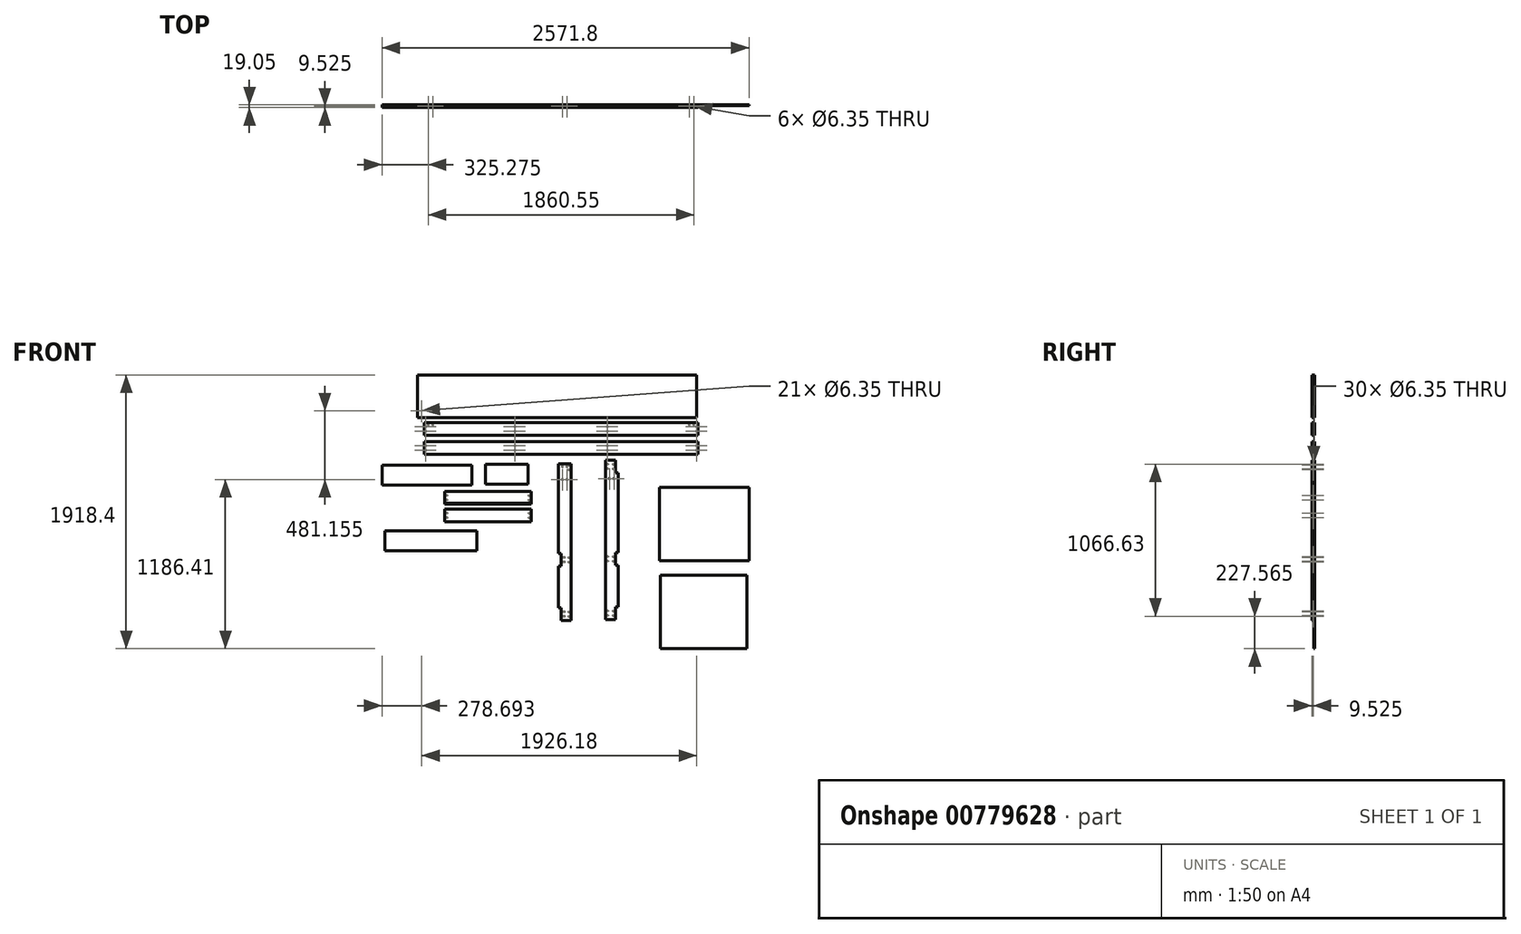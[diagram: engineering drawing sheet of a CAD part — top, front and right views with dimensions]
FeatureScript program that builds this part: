
annotation { "Feature Type Name" : "Feature", "Feature Type Description" : "" }
export const myFeature = defineFeature(function(context is Context, id is Id, definition is map)
    precondition{}
    {
        {
            var Q0;
            Q0=qCreatedBy(makeId("Front.planeOp"),FACE);
            var sketch = newSketch(context, id + "F0", { "sketchPlane" : qUnion([Q0])});
            skLineSegment(sketch, "E0.bottom", {"start": v(-0.42, -594.36) * mm, "end": v(69.43, -594.36) * mm});
            skLineSegment(sketch, "E0.left", {"start": v(-19.47, -505.46) * mm, "end": v(-19.47, -213.36) * mm});
            skLineSegment(sketch, "E0.right", {"start": v(69.43, -594.36) * mm, "end": v(69.43, 504.2) * mm});
            skLineSegment(sketch, "E1", {"start": v(-0.42, -594.36) * mm, "end": v(-0.42, -505.46) * mm});
            skLineSegment(sketch, "E2", {"start": v(-0.42, -505.46) * mm, "end": v(-19.47, -505.46) * mm});
            skLineSegment(sketch, "E3", {"start": v(-0.42, -213.36) * mm, "end": v(-19.47, -213.36) * mm});
            skLineSegment(sketch, "E4", {"start": v(-0.42, -213.36) * mm, "end": v(-0.42, -124.46) * mm});
            skLineSegment(sketch, "E5", {"start": v(-0.42, -124.46) * mm, "end": v(-19.47, -124.46) * mm});
            skLineSegment(sketch, "E6", {"start": v(-19.47, 504.2) * mm, "end": v(69.43, 504.2) * mm});
            skLineSegment(sketch, "E7", {"start": v(-19.47, -124.46) * mm, "end": v(-19.47, 504.2) * mm});
            skLineSegment(sketch, "E8", {"start": v(-0.42, -213.36) * mm, "end": v(69.43, -213.36) * mm});
            skLineSegment(sketch, "E9", {"start": v(-0.42, -124.46) * mm, "end": v(69.43, -124.46) * mm});
            skPoint(sketch, "E10", {"position": v(9.1, 393.07) * mm});
            skPoint(sketch, "E11", {"position": v(40.85, 393.07) * mm});
            skSolve(sketch);
        }
        {
            var Q0;
            Q0=qCreatedBy(makeId("Front.planeOp"),FACE);
            var sketch = newSketch(context, id + "F1", { "sketchPlane" : qUnion([Q0])});
            skLineSegment(sketch, "E12.right", {"start": v(309.74, -588.17) * mm, "end": v(309.74, 529.43) * mm});
            skLineSegment(sketch, "E13.MirrorCS", {"start": v(398.64, 440.53) * mm, "end": v(379.59, 440.53) * mm});
            skLineSegment(sketch, "E14.MirrorCS", {"start": v(379.59, -207.17) * mm, "end": v(398.64, -207.17) * mm});
            skLineSegment(sketch, "E15.MirrorCS", {"start": v(379.59, -499.27) * mm, "end": v(398.64, -499.27) * mm});
            skLineSegment(sketch, "E16.MirrorCS", {"start": v(379.59, -207.17) * mm, "end": v(379.59, -118.27) * mm});
            skLineSegment(sketch, "E17.MirrorCS", {"start": v(379.59, 440.53) * mm, "end": v(379.59, 529.43) * mm});
            skLineSegment(sketch, "E18.MirrorCS", {"start": v(379.59, -588.17) * mm, "end": v(379.59, -499.27) * mm});
            skLineSegment(sketch, "E19.MirrorCS", {"start": v(379.59, 529.43) * mm, "end": v(309.74, 529.43) * mm});
            skLineSegment(sketch, "E20.MirrorCS", {"start": v(379.59, -118.27) * mm, "end": v(398.64, -118.27) * mm});
            skLineSegment(sketch, "E21.MirrorCS", {"start": v(379.59, -588.17) * mm, "end": v(309.74, -588.17) * mm});
            skLineSegment(sketch, "E22.MirrorCS", {"start": v(398.64, -499.27) * mm, "end": v(398.64, -207.17) * mm});
            skLineSegment(sketch, "E23", {"start": v(398.64, -118.27) * mm, "end": v(398.64, 440.53) * mm});
            skLineSegment(sketch, "E24", {"start": v(379.59, -118.27) * mm, "end": v(309.74, -118.27) * mm});
            skLineSegment(sketch, "E25", {"start": v(379.59, -207.17) * mm, "end": v(309.74, -207.17) * mm});
            skPoint(sketch, "E26", {"position": v(338.31, 399.25) * mm});
            skPoint(sketch, "E27", {"position": v(370.06, 399.25) * mm});
            skSolve(sketch);
        }
        {
            var Q0;
            Q0=makeQuery(id+"F0.imprint","IMPRINT",FACE,{"disambiguationData":[TD([[makeQuery(id+"F0.imprint","IMPRINT",EDGE,{"derivedFrom":sQuery(id+"F0.wireOp",EDGE,"E0.bottom")}),1.0]])]});
            var Q1;
            Q1=makeQuery(id+"F0.imprint","IMPRINT",FACE,{"disambiguationData":[TD([[makeQuery(id+"F0.imprint","IMPRINT",EDGE,{"derivedFrom":sQuery(id+"F0.wireOp",EDGE,"E4")}),-1.0]])]});
            var Q2;
            Q2=makeQuery(id+"F0.imprint","IMPRINT",FACE,{"disambiguationData":[TD([[makeQuery(id+"F0.imprint","IMPRINT",EDGE,{"derivedFrom":sQuery(id+"F0.wireOp",EDGE,"E5")}),-1.0]])]});
            extrude(context, id + "F2", {"entities" : qUnion([Q0, Q1, Q2]), "depth" : 19.05 * mm, "offsetDistance" : 25.4 * mm});
        }
        {
            var Q0;
            Q0=makeQuery(id+"F1.imprint","IMPRINT",FACE,{"disambiguationData":[TD([[makeQuery(id+"F1.imprint","IMPRINT",EDGE,{"derivedFrom":sQuery(id+"F1.wireOp",EDGE,"E12.right")}),-1.0]])]});
            var Q1;
            Q1=makeQuery(id+"F1.imprint","IMPRINT",FACE,{"disambiguationData":[TD([[makeQuery(id+"F1.imprint","IMPRINT",EDGE,{"derivedFrom":sQuery(id+"F1.wireOp",EDGE,"E14.MirrorCS")}),-1.0]])]});
            var Q2;
            Q2=makeQuery(id+"F1.imprint","IMPRINT",FACE,{"disambiguationData":[TD([[makeQuery(id+"F1.imprint","IMPRINT",EDGE,{"derivedFrom":sQuery(id+"F1.wireOp",EDGE,"E13.MirrorCS")}),1.0]])]});
            extrude(context, id + "F3", {"entities" : qUnion([Q0, Q1, Q2]), "depth" : 19.05 * mm, "offsetDistance" : 25.4 * mm});
        }
        {
            var Q0;
            Q0=makeQuery(id+"F2.opExtrude","SWEPT_FACE",FACE,{"disambiguationData":[OSD([sQuery(id+"F0.wireOp",EDGE,"E1")])]});
            var sketch = newSketch(context, id + "F4", { "sketchPlane" : qUnion([Q0])});
            skLineSegment(sketch, "E28.0.0", {"start": v(0, -505.46) * mm, "end": v(0, -594.36) * mm});
            skLineSegment(sketch, "E28.0.1", {"start": v(0, -594.36) * mm, "end": v(19.05, -594.36) * mm});
            skLineSegment(sketch, "E28.0.2", {"start": v(19.05, -594.36) * mm, "end": v(19.05, -505.46) * mm});
            skLineSegment(sketch, "E28.0.3", {"start": v(19.05, -505.46) * mm, "end": v(0, -505.46) * mm});
            skPoint(sketch, "E29", {"position": v(9.53, -534.03) * mm});
            skPoint(sketch, "E29.positionSnap0", {"position": v(9.53, -505.46) * mm});
            skPoint(sketch, "E30", {"position": v(9.52, -565.78) * mm});
            skPoint(sketch, "E30.positionSnap0", {"position": v(9.53, -594.36) * mm});
            skSolve(sketch);
        }
        {
            var Q0;
            Q0=sQuery(id+"F4.wireOp",VERTEX,"E29");
            var Q1;
            Q1=sQuery(id+"F4.wireOp",VERTEX,"E30");
            var Q2;
            Q2=makeQuery(id+"F2.opExtrude","SWEPT_BODY",BODY,{"disambiguationData":[OSD([sQuery(id+"F0.wireOp",EDGE,"E0.bottom"),sQuery(id+"F0.wireOp",EDGE,"E0.left"),sQuery(id+"F0.wireOp",EDGE,"E0.right"),sQuery(id+"F0.wireOp",EDGE,"E1"),sQuery(id+"F0.wireOp",EDGE,"E2"),sQuery(id+"F0.wireOp",EDGE,"E3"),sQuery(id+"F0.wireOp",EDGE,"E4"),sQuery(id+"F0.wireOp",EDGE,"E5"),sQuery(id+"F0.wireOp",EDGE,"E6"),sQuery(id+"F0.wireOp",EDGE,"E7")])]});
            hole(context, id + "F5", {"style" : HoleStyle.SIMPLE, "endStyle" : HoleEndStyle.BLIND, "holeDiameter" : 6.35 * mm, "majorDiameter" : 6.35 * mm, "holeDepth" : 25.4 * mm, "isTappedThrough" : true, "tappedDepth" : 12.7 * mm, "tapClearance" : 3, "locations" : qUnion([Q0, Q1]), "scope" : qUnion([Q2])});
        }
        {
            var Q0;
            Q0=makeQuery(id+"F2.opExtrude","SWEPT_FACE",FACE,{"disambiguationData":[OSD([sQuery(id+"F0.wireOp",EDGE,"E4")])]});
            var sketch = newSketch(context, id + "F6", { "sketchPlane" : qUnion([Q0])});
            skLineSegment(sketch, "E31.0.0", {"start": v(0, -124.46) * mm, "end": v(0, -213.36) * mm});
            skLineSegment(sketch, "E31.0.1", {"start": v(0, -213.36) * mm, "end": v(19.05, -213.36) * mm});
            skLineSegment(sketch, "E31.0.2", {"start": v(19.05, -213.36) * mm, "end": v(19.05, -124.46) * mm});
            skLineSegment(sketch, "E31.0.3", {"start": v(19.05, -124.46) * mm, "end": v(0, -124.46) * mm});
            skPoint(sketch, "E32", {"position": v(9.53, -153.04) * mm});
            skPoint(sketch, "E32.positionSnap0", {"position": v(9.53, -124.46) * mm});
            skPoint(sketch, "E33", {"position": v(9.53, -184.79) * mm});
            skPoint(sketch, "E33.positionSnap0", {"position": v(9.53, -213.36) * mm});
            skSolve(sketch);
        }
        {
            var Q0;
            Q0=sQuery(id+"F6.wireOp",VERTEX,"E32");
            var Q1;
            Q1=sQuery(id+"F6.wireOp",VERTEX,"E33");
            var Q2;
            Q2=makeQuery(id+"F2.opExtrude","SWEPT_BODY",BODY,{"disambiguationData":[OSD([sQuery(id+"F0.wireOp",EDGE,"E0.bottom"),sQuery(id+"F0.wireOp",EDGE,"E0.left"),sQuery(id+"F0.wireOp",EDGE,"E0.right"),sQuery(id+"F0.wireOp",EDGE,"E1"),sQuery(id+"F0.wireOp",EDGE,"E2"),sQuery(id+"F0.wireOp",EDGE,"E3"),sQuery(id+"F0.wireOp",EDGE,"E4"),sQuery(id+"F0.wireOp",EDGE,"E5"),sQuery(id+"F0.wireOp",EDGE,"E6"),sQuery(id+"F0.wireOp",EDGE,"E7")])]});
            hole(context, id + "F7", {"style" : HoleStyle.SIMPLE, "endStyle" : HoleEndStyle.BLIND, "holeDiameter" : 6.35 * mm, "majorDiameter" : 6.35 * mm, "holeDepth" : 25.4 * mm, "isTappedThrough" : true, "tappedDepth" : 12.7 * mm, "tapClearance" : 3, "locations" : qUnion([Q0, Q1]), "scope" : qUnion([Q2])});
        }
        {
            var Q0;
            Q0=makeQuery(id+"F2.opExtrude","SWEPT_FACE",FACE,{"disambiguationData":[OSD([sQuery(id+"F0.wireOp",EDGE,"E0.right")])]});
            var sketch = newSketch(context, id + "F8", { "sketchPlane" : qUnion([Q0])});
            skLineSegment(sketch, "E34.0.0", {"start": v(0, -594.36) * mm, "end": v(0, 504.2) * mm});
            skLineSegment(sketch, "E34.0.1", {"start": v(0, 504.2) * mm, "end": v(-19.05, 504.2) * mm});
            skLineSegment(sketch, "E34.0.2", {"start": v(-19.05, 504.2) * mm, "end": v(-19.05, -594.36) * mm});
            skLineSegment(sketch, "E34.0.3", {"start": v(-19.05, -594.36) * mm, "end": v(0, -594.36) * mm});
            skPoint(sketch, "E35", {"position": v(-9.53, 494.67) * mm});
            skPoint(sketch, "E35.positionSnap0", {"position": v(-9.53, 504.2) * mm});
            skPoint(sketch, "E36", {"position": v(-9.53, 462.92) * mm});
            skPoint(sketch, "E37", {"position": v(-9.53, -565.78) * mm});
            skPoint(sketch, "E37.positionSnap0", {"position": v(-9.53, -594.36) * mm});
            skPoint(sketch, "E38", {"position": v(-9.53, -534.03) * mm});
            skPoint(sketch, "E39.0", {"position": v(0, -124.46) * mm});
            skPoint(sketch, "E40.0", {"position": v(0, -213.36) * mm});
            skPoint(sketch, "E41", {"position": v(-9.53, -213.36) * mm});
            skPoint(sketch, "E42", {"position": v(-9.53, -184.79) * mm});
            skPoint(sketch, "E43", {"position": v(-9.53, -153.04) * mm});
            skSolve(sketch);
        }
        {
            var Q0;
            Q0=sQuery(id+"F8.wireOp",VERTEX,"E35");
            var Q1;
            Q1=sQuery(id+"F8.wireOp",VERTEX,"E36");
            var Q2;
            Q2=sQuery(id+"F8.wireOp",VERTEX,"E37");
            var Q3;
            Q3=sQuery(id+"F8.wireOp",VERTEX,"E38");
            var Q4;
            Q4=sQuery(id+"F8.wireOp",VERTEX,"E42");
            var Q5;
            Q5=sQuery(id+"F8.wireOp",VERTEX,"E43");
            var Q6;
            Q6=makeQuery(id+"F2.opExtrude","SWEPT_BODY",BODY,{"disambiguationData":[OSD([sQuery(id+"F0.wireOp",EDGE,"E0.bottom"),sQuery(id+"F0.wireOp",EDGE,"E0.left"),sQuery(id+"F0.wireOp",EDGE,"E0.right"),sQuery(id+"F0.wireOp",EDGE,"E1"),sQuery(id+"F0.wireOp",EDGE,"E2"),sQuery(id+"F0.wireOp",EDGE,"E3"),sQuery(id+"F0.wireOp",EDGE,"E4"),sQuery(id+"F0.wireOp",EDGE,"E5"),sQuery(id+"F0.wireOp",EDGE,"E6"),sQuery(id+"F0.wireOp",EDGE,"E7")])]});
            hole(context, id + "F9", {"style" : HoleStyle.SIMPLE, "endStyle" : HoleEndStyle.BLIND, "holeDiameter" : 6.35 * mm, "majorDiameter" : 6.35 * mm, "holeDepth" : 19.05 * mm, "isTappedThrough" : true, "tappedDepth" : 12.7 * mm, "tapClearance" : 3, "locations" : qUnion([Q0, Q1, Q2, Q3, Q4, Q5]), "scope" : qUnion([Q6])});
        }
        {
            var Q0;
            Q0=makeQuery(id+"F2.opExtrude","SWEPT_FACE",FACE,{"disambiguationData":[OSD([sQuery(id+"F0.wireOp",EDGE,"E6")])]});
            var sketch = newSketch(context, id + "F10", { "sketchPlane" : qUnion([Q0])});
            skLineSegment(sketch, "E44.0.0", {"start": v(69.43, 0) * mm, "end": v(-19.47, 0) * mm});
            skLineSegment(sketch, "E44.0.1", {"start": v(-19.47, 0) * mm, "end": v(-19.47, -19.05) * mm});
            skLineSegment(sketch, "E44.0.2", {"start": v(-19.47, -19.05) * mm, "end": v(69.43, -19.05) * mm});
            skLineSegment(sketch, "E44.0.3", {"start": v(69.43, -19.05) * mm, "end": v(69.43, 0) * mm});
            skPoint(sketch, "E45", {"position": v(9.1, -9.53) * mm});
            skPoint(sketch, "E45.positionSnap0", {"position": v(-19.47, -9.53) * mm});
            skPoint(sketch, "E46", {"position": v(40.85, -9.53) * mm});
            skSolve(sketch);
        }
        {
            var Q0;
            Q0=sQuery(id+"F10.wireOp",VERTEX,"E45");
            var Q1;
            Q1=sQuery(id+"F10.wireOp",VERTEX,"E46");
            var Q2;
            Q2=makeQuery(id+"F2.opExtrude","SWEPT_BODY",BODY,{"disambiguationData":[OSD([sQuery(id+"F0.wireOp",EDGE,"E0.bottom"),sQuery(id+"F0.wireOp",EDGE,"E0.left"),sQuery(id+"F0.wireOp",EDGE,"E0.right"),sQuery(id+"F0.wireOp",EDGE,"E1"),sQuery(id+"F0.wireOp",EDGE,"E2"),sQuery(id+"F0.wireOp",EDGE,"E3"),sQuery(id+"F0.wireOp",EDGE,"E4"),sQuery(id+"F0.wireOp",EDGE,"E5"),sQuery(id+"F0.wireOp",EDGE,"E6"),sQuery(id+"F0.wireOp",EDGE,"E7")])]});
            hole(context, id + "F11", {"style" : HoleStyle.SIMPLE, "endStyle" : HoleEndStyle.BLIND, "holeDiameter" : 6.35 * mm, "majorDiameter" : 6.35 * mm, "holeDepth" : 25.4 * mm, "isTappedThrough" : true, "tappedDepth" : 12.7 * mm, "tapClearance" : 3, "locations" : qUnion([Q0, Q1]), "scope" : qUnion([Q2])});
        }
        {
            var Q0;
            Q0=makeQuery(id+"F3.opExtrude","SWEPT_FACE",FACE,{"disambiguationData":[OSD([sQuery(id+"F1.wireOp",EDGE,"E17.MirrorCS")])]});
            var sketch = newSketch(context, id + "F12", { "sketchPlane" : qUnion([Q0])});
            skLineSegment(sketch, "E47.0.0", {"start": v(0, 440.53) * mm, "end": v(0, 529.43) * mm});
            skLineSegment(sketch, "E47.0.1", {"start": v(0, 529.43) * mm, "end": v(-19.05, 529.43) * mm});
            skLineSegment(sketch, "E47.0.2", {"start": v(-19.05, 529.43) * mm, "end": v(-19.05, 440.53) * mm});
            skLineSegment(sketch, "E47.0.3", {"start": v(-19.05, 440.53) * mm, "end": v(0, 440.53) * mm});
            skPoint(sketch, "E48", {"position": v(-9.53, 529.43) * mm});
            skPoint(sketch, "E49", {"position": v(-9.53, 500.85) * mm});
            skPoint(sketch, "E50", {"position": v(-9.53, 469.1) * mm});
            skSolve(sketch);
        }
        {
            var Q0;
            Q0=sQuery(id+"F12.wireOp",VERTEX,"E49");
            var Q1;
            Q1=sQuery(id+"F12.wireOp",VERTEX,"E50");
            var Q2;
            Q2=makeQuery(id+"F3.opExtrude","SWEPT_BODY",BODY,{"disambiguationData":[OSD([sQuery(id+"F1.wireOp",EDGE,"E12.right"),sQuery(id+"F1.wireOp",EDGE,"E13.MirrorCS"),sQuery(id+"F1.wireOp",EDGE,"E14.MirrorCS"),sQuery(id+"F1.wireOp",EDGE,"E15.MirrorCS"),sQuery(id+"F1.wireOp",EDGE,"E16.MirrorCS"),sQuery(id+"F1.wireOp",EDGE,"E17.MirrorCS"),sQuery(id+"F1.wireOp",EDGE,"E18.MirrorCS"),sQuery(id+"F1.wireOp",EDGE,"E19.MirrorCS"),sQuery(id+"F1.wireOp",EDGE,"E20.MirrorCS"),sQuery(id+"F1.wireOp",EDGE,"E21.MirrorCS"),sQuery(id+"F1.wireOp",EDGE,"E22.MirrorCS"),sQuery(id+"F1.wireOp",EDGE,"E23")])]});
            hole(context, id + "F13", {"style" : HoleStyle.SIMPLE, "endStyle" : HoleEndStyle.BLIND, "holeDiameter" : 6.35 * mm, "majorDiameter" : 6.35 * mm, "holeDepth" : 19.05 * mm, "isTappedThrough" : true, "tappedDepth" : 12.7 * mm, "tapClearance" : 3, "locations" : qUnion([Q0, Q1]), "scope" : qUnion([Q2])});
        }
        {
            var Q0;
            Q0=makeQuery(id+"F3.opExtrude","SWEPT_FACE",FACE,{"disambiguationData":[OSD([sQuery(id+"F1.wireOp",EDGE,"E16.MirrorCS")])]});
            var sketch = newSketch(context, id + "F14", { "sketchPlane" : qUnion([Q0])});
            skLineSegment(sketch, "E51.0.0", {"start": v(0, -207.17) * mm, "end": v(0, -118.27) * mm});
            skLineSegment(sketch, "E51.0.1", {"start": v(0, -118.27) * mm, "end": v(-19.05, -118.27) * mm});
            skLineSegment(sketch, "E51.0.2", {"start": v(-19.05, -118.27) * mm, "end": v(-19.05, -207.17) * mm});
            skLineSegment(sketch, "E51.0.3", {"start": v(-19.05, -207.17) * mm, "end": v(0, -207.17) * mm});
            skPoint(sketch, "E52", {"position": v(-9.53, -118.27) * mm});
            skPoint(sketch, "E53", {"position": v(-9.53, -146.85) * mm});
            skPoint(sketch, "E54", {"position": v(-9.53, -207.17) * mm});
            skPoint(sketch, "E55", {"position": v(-9.53, -178.6) * mm});
            skSolve(sketch);
        }
        {
            var Q0;
            Q0=sQuery(id+"F14.wireOp",VERTEX,"E53");
            var Q1;
            Q1=sQuery(id+"F14.wireOp",VERTEX,"E55");
            var Q2;
            Q2=makeQuery(id+"F3.opExtrude","SWEPT_BODY",BODY,{"disambiguationData":[OSD([sQuery(id+"F1.wireOp",EDGE,"E12.right"),sQuery(id+"F1.wireOp",EDGE,"E13.MirrorCS"),sQuery(id+"F1.wireOp",EDGE,"E14.MirrorCS"),sQuery(id+"F1.wireOp",EDGE,"E15.MirrorCS"),sQuery(id+"F1.wireOp",EDGE,"E16.MirrorCS"),sQuery(id+"F1.wireOp",EDGE,"E17.MirrorCS"),sQuery(id+"F1.wireOp",EDGE,"E18.MirrorCS"),sQuery(id+"F1.wireOp",EDGE,"E19.MirrorCS"),sQuery(id+"F1.wireOp",EDGE,"E20.MirrorCS"),sQuery(id+"F1.wireOp",EDGE,"E21.MirrorCS"),sQuery(id+"F1.wireOp",EDGE,"E22.MirrorCS"),sQuery(id+"F1.wireOp",EDGE,"E23")])]});
            hole(context, id + "F15", {"style" : HoleStyle.SIMPLE, "endStyle" : HoleEndStyle.BLIND, "holeDiameter" : 6.35 * mm, "majorDiameter" : 6.35 * mm, "holeDepth" : 19.05 * mm, "isTappedThrough" : true, "tappedDepth" : 12.7 * mm, "tapClearance" : 3, "locations" : qUnion([Q0, Q1]), "scope" : qUnion([Q2])});
        }
        {
            var Q0;
            Q0=makeQuery(id+"F3.opExtrude","SWEPT_FACE",FACE,{"disambiguationData":[OSD([sQuery(id+"F1.wireOp",EDGE,"E18.MirrorCS")])]});
            var sketch = newSketch(context, id + "F16", { "sketchPlane" : qUnion([Q0])});
            skLineSegment(sketch, "E56.0.0", {"start": v(0, -588.17) * mm, "end": v(0, -499.27) * mm});
            skLineSegment(sketch, "E56.0.1", {"start": v(0, -499.27) * mm, "end": v(-19.05, -499.27) * mm});
            skLineSegment(sketch, "E56.0.2", {"start": v(-19.05, -499.27) * mm, "end": v(-19.05, -588.17) * mm});
            skLineSegment(sketch, "E56.0.3", {"start": v(-19.05, -588.17) * mm, "end": v(0, -588.17) * mm});
            skPoint(sketch, "E57", {"position": v(-9.53, -527.85) * mm});
            skPoint(sketch, "E57.positionSnap0", {"position": v(-9.53, -499.27) * mm});
            skPoint(sketch, "E58", {"position": v(-9.53, -559.6) * mm});
            skPoint(sketch, "E58.positionSnap0", {"position": v(-9.53, -588.17) * mm});
            skSolve(sketch);
        }
        {
            var Q0;
            Q0=sQuery(id+"F16.wireOp",VERTEX,"E57");
            var Q1;
            Q1=sQuery(id+"F16.wireOp",VERTEX,"E58");
            var Q2;
            Q2=makeQuery(id+"F3.opExtrude","SWEPT_BODY",BODY,{"disambiguationData":[OSD([sQuery(id+"F1.wireOp",EDGE,"E12.right"),sQuery(id+"F1.wireOp",EDGE,"E13.MirrorCS"),sQuery(id+"F1.wireOp",EDGE,"E14.MirrorCS"),sQuery(id+"F1.wireOp",EDGE,"E15.MirrorCS"),sQuery(id+"F1.wireOp",EDGE,"E16.MirrorCS"),sQuery(id+"F1.wireOp",EDGE,"E17.MirrorCS"),sQuery(id+"F1.wireOp",EDGE,"E18.MirrorCS"),sQuery(id+"F1.wireOp",EDGE,"E19.MirrorCS"),sQuery(id+"F1.wireOp",EDGE,"E20.MirrorCS"),sQuery(id+"F1.wireOp",EDGE,"E21.MirrorCS"),sQuery(id+"F1.wireOp",EDGE,"E22.MirrorCS"),sQuery(id+"F1.wireOp",EDGE,"E23")])]});
            hole(context, id + "F17", {"style" : HoleStyle.SIMPLE, "endStyle" : HoleEndStyle.BLIND, "holeDiameter" : 6.35 * mm, "majorDiameter" : 6.35 * mm, "holeDepth" : 19.05 * mm, "isTappedThrough" : true, "tappedDepth" : 12.7 * mm, "tapClearance" : 3, "locations" : qUnion([Q0, Q1]), "scope" : qUnion([Q2])});
        }
        {
            var Q0;
            Q0=makeQuery(id+"F3.opExtrude","SWEPT_FACE",FACE,{"disambiguationData":[OSD([sQuery(id+"F1.wireOp",EDGE,"E12.right")])]});
            var sketch = newSketch(context, id + "F18", { "sketchPlane" : qUnion([Q0])});
            skLineSegment(sketch, "E59.0.0", {"start": v(0, 529.43) * mm, "end": v(0, -588.17) * mm});
            skLineSegment(sketch, "E59.0.1", {"start": v(0, -588.17) * mm, "end": v(19.05, -588.17) * mm});
            skLineSegment(sketch, "E59.0.2", {"start": v(19.05, -588.17) * mm, "end": v(19.05, 529.43) * mm});
            skLineSegment(sketch, "E59.0.3", {"start": v(19.05, 529.43) * mm, "end": v(0, 529.43) * mm});
            skPoint(sketch, "E60.0", {"position": v(0, -118.27) * mm});
            skPoint(sketch, "E61.0", {"position": v(0, -207.17) * mm});
            skPoint(sketch, "E62", {"position": v(9.53, 500.85) * mm});
            skPoint(sketch, "E62.positionSnap0", {"position": v(9.53, 529.43) * mm});
            skPoint(sketch, "E63", {"position": v(9.53, 469.1) * mm});
            skLineSegment(sketch, "E64", {"start": v(0, -118.27) * mm, "end": v(19.05, -118.27) * mm});
            skLineSegment(sketch, "E65", {"start": v(0, -207.17) * mm, "end": v(19.05, -207.17) * mm});
            skPoint(sketch, "E66", {"position": v(9.53, -146.85) * mm});
            skPoint(sketch, "E66.positionSnap0", {"position": v(9.53, -118.27) * mm});
            skPoint(sketch, "E67", {"position": v(9.52, -178.6) * mm});
            skPoint(sketch, "E67.positionSnap0", {"position": v(9.53, -207.17) * mm});
            skPoint(sketch, "E68", {"position": v(9.52, -559.6) * mm});
            skPoint(sketch, "E68.positionSnap0", {"position": v(9.53, -588.17) * mm});
            skPoint(sketch, "E69", {"position": v(9.52, -527.85) * mm});
            skSolve(sketch);
        }
        {
            var Q0;
            Q0=sQuery(id+"F18.wireOp",VERTEX,"E68");
            var Q1;
            Q1=sQuery(id+"F18.wireOp",VERTEX,"E69");
            var Q2;
            Q2=sQuery(id+"F18.wireOp",VERTEX,"E66");
            var Q3;
            Q3=sQuery(id+"F18.wireOp",VERTEX,"E67");
            var Q4;
            Q4=sQuery(id+"F18.wireOp",VERTEX,"E62");
            var Q5;
            Q5=sQuery(id+"F18.wireOp",VERTEX,"E63");
            var Q6;
            Q6=makeQuery(id+"F3.opExtrude","SWEPT_BODY",BODY,{"disambiguationData":[OSD([sQuery(id+"F1.wireOp",EDGE,"E12.right"),sQuery(id+"F1.wireOp",EDGE,"E13.MirrorCS"),sQuery(id+"F1.wireOp",EDGE,"E14.MirrorCS"),sQuery(id+"F1.wireOp",EDGE,"E15.MirrorCS"),sQuery(id+"F1.wireOp",EDGE,"E16.MirrorCS"),sQuery(id+"F1.wireOp",EDGE,"E17.MirrorCS"),sQuery(id+"F1.wireOp",EDGE,"E18.MirrorCS"),sQuery(id+"F1.wireOp",EDGE,"E19.MirrorCS"),sQuery(id+"F1.wireOp",EDGE,"E20.MirrorCS"),sQuery(id+"F1.wireOp",EDGE,"E21.MirrorCS"),sQuery(id+"F1.wireOp",EDGE,"E22.MirrorCS"),sQuery(id+"F1.wireOp",EDGE,"E23")])]});
            hole(context, id + "F19", {"style" : HoleStyle.SIMPLE, "endStyle" : HoleEndStyle.BLIND, "holeDiameter" : 6.35 * mm, "majorDiameter" : 6.35 * mm, "holeDepth" : 19.05 * mm, "isTappedThrough" : true, "tappedDepth" : 12.7 * mm, "tapClearance" : 3, "locations" : qUnion([Q0, Q1, Q2, Q3, Q4, Q5]), "scope" : qUnion([Q6])});
        }
        {
            var Q0;
            Q0=qCreatedBy(makeId("Front.planeOp"),FACE);
            var sketch = newSketch(context, id + "F20", { "sketchPlane" : qUnion([Q0])});
            skLineSegment(sketch, "E70.bottom", {"start": v(-958.85, 657.8) * mm, "end": v(958.85, 657.8) * mm});
            skLineSegment(sketch, "E70.top", {"start": v(-958.85, 568.9) * mm, "end": v(958.85, 568.9) * mm});
            skLineSegment(sketch, "E70.left", {"start": v(-958.85, 657.8) * mm, "end": v(-958.85, 568.9) * mm});
            skLineSegment(sketch, "E70.right", {"start": v(958.85, 657.8) * mm, "end": v(958.85, 568.9) * mm});
            skPoint(sketch, "E71", {"position": v(-949.32, 629.22) * mm});
            skPoint(sketch, "E72", {"position": v(-949.32, 597.47) * mm});
            skPoint(sketch, "E73", {"position": v(949.33, 629.22) * mm});
            skPoint(sketch, "E74", {"position": v(949.33, 597.47) * mm});
            skPoint(sketch, "E75", {"position": v(-323.85, 629.22) * mm});
            skPoint(sketch, "E76", {"position": v(-323.85, 597.47) * mm});
            skPoint(sketch, "E77", {"position": v(323.85, 629.22) * mm});
            skPoint(sketch, "E78", {"position": v(323.85, 597.47) * mm});
            skSolve(sketch);
        }
        {
            var Q0;
            Q0=makeQuery(id+"F20.imprint","IMPRINT",FACE,{"disambiguationData":[TD([[makeQuery(id+"F20.imprint","IMPRINT",EDGE,{"derivedFrom":sQuery(id+"F20.wireOp",EDGE,"E70.bottom")}),-1.0]])]});
            extrude(context, id + "F21", {"entities" : qUnion([Q0]), "depth" : 19.05 * mm, "offsetDistance" : 25.4 * mm});
        }
        {
            var Q0;
            Q0=sQuery(id+"F20.wireOp",VERTEX,"E71");
            var Q1;
            Q1=sQuery(id+"F20.wireOp",VERTEX,"E72");
            var Q2;
            Q2=sQuery(id+"F20.wireOp",VERTEX,"E75");
            var Q3;
            Q3=sQuery(id+"F20.wireOp",VERTEX,"E76");
            var Q4;
            Q4=sQuery(id+"F20.wireOp",VERTEX,"E77");
            var Q5;
            Q5=sQuery(id+"F20.wireOp",VERTEX,"E78");
            var Q6;
            Q6=sQuery(id+"F20.wireOp",VERTEX,"E73");
            var Q7;
            Q7=sQuery(id+"F20.wireOp",VERTEX,"E74");
            var Q8;
            Q8=makeQuery(id+"F21.opExtrude","SWEPT_BODY",BODY,{"disambiguationData":[OSD([sQuery(id+"F20.wireOp",EDGE,"E70.bottom"),sQuery(id+"F20.wireOp",EDGE,"E70.top"),sQuery(id+"F20.wireOp",EDGE,"E70.left"),sQuery(id+"F20.wireOp",EDGE,"E70.right")])]});
            hole(context, id + "F22", {"style" : HoleStyle.SIMPLE, "endStyle" : HoleEndStyle.THROUGH, "oppositeDirection" : true, "holeDiameter" : 6.35 * mm, "majorDiameter" : 6.35 * mm, "isTappedThrough" : true, "tappedDepth" : 12.7 * mm, "tapClearance" : 3, "locations" : qUnion([Q0, Q1, Q2, Q3, Q4, Q5, Q6, Q7]), "scope" : qUnion([Q8])});
        }
        {
            var Q0;
            Q0=qCreatedBy(makeId("Front.planeOp"),FACE);
            var sketch = newSketch(context, id + "F23", { "sketchPlane" : qUnion([Q0])});
            skLineSegment(sketch, "E79.bottom", {"start": v(-958.85, 791.08) * mm, "end": v(958.85, 791.08) * mm});
            skLineSegment(sketch, "E79.top", {"start": v(-958.85, 702.18) * mm, "end": v(958.85, 702.18) * mm});
            skLineSegment(sketch, "E79.left", {"start": v(-958.85, 791.08) * mm, "end": v(-958.85, 702.18) * mm});
            skLineSegment(sketch, "E79.right", {"start": v(958.85, 791.08) * mm, "end": v(958.85, 702.18) * mm});
            skPoint(sketch, "E80", {"position": v(-949.33, 762.5) * mm});
            skPoint(sketch, "E81", {"position": v(-949.33, 730.75) * mm});
            skPoint(sketch, "E82", {"position": v(949.33, 762.5) * mm});
            skPoint(sketch, "E83", {"position": v(949.32, 730.75) * mm});
            skPoint(sketch, "E84", {"position": v(-323.85, 762.5) * mm});
            skPoint(sketch, "E85", {"position": v(-323.85, 730.75) * mm});
            skPoint(sketch, "E86", {"position": v(323.85, 762.5) * mm});
            skPoint(sketch, "E87", {"position": v(323.85, 730.75) * mm});
            skSolve(sketch);
        }
        {
            var Q0;
            Q0=makeQuery(id+"F23.imprint","IMPRINT",FACE,{"disambiguationData":[TD([[makeQuery(id+"F23.imprint","IMPRINT",EDGE,{"derivedFrom":sQuery(id+"F23.wireOp",EDGE,"E79.bottom")}),-1.0]])]});
            extrude(context, id + "F24", {"entities" : qUnion([Q0]), "depth" : 19.05 * mm, "offsetDistance" : 25.4 * mm});
        }
        {
            var Q0;
            Q0=sQuery(id+"F23.wireOp",VERTEX,"E80");
            var Q1;
            Q1=sQuery(id+"F23.wireOp",VERTEX,"E81");
            var Q2;
            Q2=sQuery(id+"F23.wireOp",VERTEX,"E84");
            var Q3;
            Q3=sQuery(id+"F23.wireOp",VERTEX,"E85");
            var Q4;
            Q4=sQuery(id+"F23.wireOp",VERTEX,"E86");
            var Q5;
            Q5=sQuery(id+"F23.wireOp",VERTEX,"E87");
            var Q6;
            Q6=sQuery(id+"F23.wireOp",VERTEX,"E83");
            var Q7;
            Q7=sQuery(id+"F23.wireOp",VERTEX,"E82");
            var Q8;
            Q8=makeQuery(id+"F24.opExtrude","SWEPT_BODY",BODY,{"disambiguationData":[OSD([sQuery(id+"F23.wireOp",EDGE,"E79.bottom"),sQuery(id+"F23.wireOp",EDGE,"E79.top"),sQuery(id+"F23.wireOp",EDGE,"E79.left"),sQuery(id+"F23.wireOp",EDGE,"E79.right")])]});
            hole(context, id + "F25", {"style" : HoleStyle.SIMPLE, "endStyle" : HoleEndStyle.THROUGH, "oppositeDirection" : true, "holeDiameter" : 6.35 * mm, "majorDiameter" : 6.35 * mm, "isTappedThrough" : true, "tappedDepth" : 12.7 * mm, "tapClearance" : 3, "locations" : qUnion([Q0, Q1, Q2, Q3, Q4, Q5, Q6, Q7]), "scope" : qUnion([Q8])});
        }
        {
            var Q0;
            Q0=makeQuery(id+"F24.opExtrude","SWEPT_FACE",FACE,{"disambiguationData":[OSD([sQuery(id+"F23.wireOp",EDGE,"E79.bottom")])]});
            var sketch = newSketch(context, id + "F26", { "sketchPlane" : qUnion([Q0])});
            skPoint(sketch, "E88", {"position": v(-930.27, -9.53) * mm});
            skPoint(sketch, "E88.positionSnap0", {"position": v(-958.85, -9.53) * mm});
            skPoint(sketch, "E89", {"position": v(-898.52, -9.53) * mm});
            skPoint(sketch, "E90", {"position": v(930.27, -9.52) * mm});
            skPoint(sketch, "E91", {"position": v(898.52, -9.52) * mm});
            skSolve(sketch);
        }
        {
            var Q0;
            Q0=sQuery(id+"F26.wireOp",VERTEX,"E88");
            var Q1;
            Q1=sQuery(id+"F26.wireOp",VERTEX,"E89");
            var Q2;
            Q2=sQuery(id+"F26.wireOp",VERTEX,"E91");
            var Q3;
            Q3=sQuery(id+"F26.wireOp",VERTEX,"E90");
            var Q4;
            Q4=makeQuery(id+"F24.opExtrude","SWEPT_BODY",BODY,{"disambiguationData":[OSD([sQuery(id+"F23.wireOp",EDGE,"E79.bottom"),sQuery(id+"F23.wireOp",EDGE,"E79.top"),sQuery(id+"F23.wireOp",EDGE,"E79.left"),sQuery(id+"F23.wireOp",EDGE,"E79.right")])]});
            hole(context, id + "F27", {"style" : HoleStyle.SIMPLE, "endStyle" : HoleEndStyle.BLIND, "holeDiameter" : 6.35 * mm, "majorDiameter" : 6.35 * mm, "holeDepth" : 19.05 * mm, "isTappedThrough" : true, "tappedDepth" : 12.7 * mm, "tapClearance" : 3, "locations" : qUnion([Q0, Q1, Q2, Q3]), "scope" : qUnion([Q4])});
        }
        {
            var Q0;
            Q0=qCreatedBy(makeId("Front.planeOp"),FACE);
            var sketch = newSketch(context, id + "F28", { "sketchPlane" : qUnion([Q0])});
            skLineSegment(sketch, "E92.bottom", {"start": v(-529.1, 498) * mm, "end": v(-230.65, 498) * mm});
            skLineSegment(sketch, "E92.top", {"start": v(-529.1, 358.3) * mm, "end": v(-230.65, 358.3) * mm});
            skLineSegment(sketch, "E92.left", {"start": v(-529.1, 498) * mm, "end": v(-529.1, 358.3) * mm});
            skLineSegment(sketch, "E92.right", {"start": v(-230.65, 498) * mm, "end": v(-230.65, 358.3) * mm});
            skSolve(sketch);
        }
        {
            var Q0;
            Q0=makeQuery(id+"F28.imprint","IMPRINT",FACE,{"disambiguationData":[TD([[makeQuery(id+"F28.imprint","IMPRINT",EDGE,{"derivedFrom":sQuery(id+"F28.wireOp",EDGE,"E92.bottom")}),-1.0]])]});
            extrude(context, id + "F29", {"entities" : qUnion([Q0]), "depth" : 19.05 * mm, "offsetDistance" : 25.4 * mm});
        }
        {
            var Q0;
            Q0=sQuery(id+"F0.wireOp",VERTEX,"E10");
            var Q1;
            Q1=sQuery(id+"F0.wireOp",VERTEX,"E11");
            var Q2;
            Q2=makeQuery(id+"F2.opExtrude","SWEPT_BODY",BODY,{"disambiguationData":[OSD([sQuery(id+"F0.wireOp",EDGE,"E0.bottom"),sQuery(id+"F0.wireOp",EDGE,"E0.left"),sQuery(id+"F0.wireOp",EDGE,"E0.right"),sQuery(id+"F0.wireOp",EDGE,"E1"),sQuery(id+"F0.wireOp",EDGE,"E2"),sQuery(id+"F0.wireOp",EDGE,"E3"),sQuery(id+"F0.wireOp",EDGE,"E4"),sQuery(id+"F0.wireOp",EDGE,"E5"),sQuery(id+"F0.wireOp",EDGE,"E6"),sQuery(id+"F0.wireOp",EDGE,"E7")])]});
            hole(context, id + "F30", {"style" : HoleStyle.SIMPLE, "endStyle" : HoleEndStyle.THROUGH, "oppositeDirection" : true, "holeDiameter" : 6.35 * mm, "majorDiameter" : 6.35 * mm, "isTappedThrough" : true, "tappedDepth" : 12.7 * mm, "tapClearance" : 3, "locations" : qUnion([Q0, Q1]), "scope" : qUnion([Q2])});
        }
        {
            var Q0;
            Q0=qCreatedBy(makeId("Front.planeOp"),FACE);
            var sketch = newSketch(context, id + "F31", { "sketchPlane" : qUnion([Q0])});
            skLineSegment(sketch, "E93.bottom", {"start": v(-817.43, 309.7) * mm, "end": v(-211, 309.7) * mm});
            skLineSegment(sketch, "E93.top", {"start": v(-817.43, 220.8) * mm, "end": v(-211, 220.8) * mm});
            skLineSegment(sketch, "E93.left", {"start": v(-817.43, 309.7) * mm, "end": v(-817.43, 220.8) * mm});
            skLineSegment(sketch, "E93.right", {"start": v(-211, 309.7) * mm, "end": v(-211, 220.8) * mm});
            skLineSegment(sketch, "E94", {"start": v(-817.43, 220.8) * mm, "end": v(-817.43, 227.14) * mm});
            skLineSegment(sketch, "E95", {"start": v(-817.43, 227.14) * mm, "end": v(-211, 227.14) * mm});
            skSolve(sketch);
        }
        {
            var Q0;
            Q0=makeQuery(id+"F31.imprint","IMPRINT",FACE,{"disambiguationData":[TD([[makeQuery(id+"F31.imprint","IMPRINT",EDGE,{"derivedFrom":sQuery(id+"F31.wireOp",EDGE,"E93.bottom")}),-1.0]])]});
            extrude(context, id + "F32", {"entities" : qUnion([Q0]), "depth" : 19.05 * mm, "offsetDistance" : 25.4 * mm});
        }
        {
            var Q0;
            Q0=makeQuery(id+"F32.opExtrude","SWEPT_FACE",FACE,{"disambiguationData":[OSD([sQuery(id+"F31.wireOp",EDGE,"E93.left")])]});
            var sketch = newSketch(context, id + "F33", { "sketchPlane" : qUnion([Q0])});
            skLineSegment(sketch, "E96.0", {"start": v(0, 309.7) * mm, "end": v(0, 309.7) * mm});
            skLineSegment(sketch, "E97.0", {"start": v(19.05, 309.7) * mm, "end": v(19.05, 309.7) * mm});
            skLineSegment(sketch, "E98.0.1", {"start": v(19.05, 309.7) * mm, "end": v(0, 309.7) * mm});
            skLineSegment(sketch, "E98.0.3", {"start": v(19.05, 309.7) * mm, "end": v(0, 309.7) * mm});
            skPoint(sketch, "E99", {"position": v(9.53, 281.12) * mm});
            skPoint(sketch, "E99.positionSnap0", {"position": v(9.53, 309.7) * mm});
            skPoint(sketch, "E100", {"position": v(9.53, 249.37) * mm});
            skSolve(sketch);
        }
        {
            var Q0;
            Q0=sQuery(id+"F33.wireOp",VERTEX,"E99");
            var Q1;
            Q1=sQuery(id+"F33.wireOp",VERTEX,"E99");
            var Q2;
            Q2=makeQuery(id+"F32.opExtrude","SWEPT_BODY",BODY,{"disambiguationData":[OSD([sQuery(id+"F31.wireOp",EDGE,"E93.bottom"),sQuery(id+"F31.wireOp",EDGE,"E93.top"),sQuery(id+"F31.wireOp",EDGE,"E93.left"),sQuery(id+"F31.wireOp",EDGE,"E93.right")])]});
            hole(context, id + "F34", {"style" : HoleStyle.SIMPLE, "endStyle" : HoleEndStyle.BLIND, "holeDiameter" : 6.35 * mm, "majorDiameter" : 6.35 * mm, "holeDepth" : 19.05 * mm, "isTappedThrough" : true, "tappedDepth" : 12.7 * mm, "tapClearance" : 3, "locations" : qUnion([Q0, Q1]), "scope" : qUnion([Q2])});
        }
        {
            var Q0;
            Q0=makeQuery(id+"F32.opExtrude","SWEPT_FACE",FACE,{"disambiguationData":[OSD([sQuery(id+"F31.wireOp",EDGE,"E93.right")])]});
            var sketch = newSketch(context, id + "F35", { "sketchPlane" : qUnion([Q0])});
            skLineSegment(sketch, "E101.0.0", {"start": v(0, 309.7) * mm, "end": v(0, 309.7) * mm});
            skLineSegment(sketch, "E101.0.1", {"start": v(0, 309.7) * mm, "end": v(-19.05, 309.7) * mm});
            skLineSegment(sketch, "E101.0.2", {"start": v(-19.05, 309.7) * mm, "end": v(-19.05, 309.7) * mm});
            skLineSegment(sketch, "E101.0.3", {"start": v(0, 309.7) * mm, "end": v(-19.05, 309.7) * mm});
            skPoint(sketch, "E102", {"position": v(-9.53, 281.12) * mm});
            skPoint(sketch, "E102.positionSnap0", {"position": v(-9.53, 309.7) * mm});
            skPoint(sketch, "E103", {"position": v(-9.52, 281.12) * mm});
            skPoint(sketch, "E104", {"position": v(-9.53, 249.37) * mm});
            skSolve(sketch);
        }
        {
            var Q0;
            Q0=sQuery(id+"F35.wireOp",VERTEX,"E102");
            var Q1;
            Q1=sQuery(id+"F35.wireOp",VERTEX,"E103");
            var Q2;
            Q2=makeQuery(id+"F32.opExtrude","SWEPT_BODY",BODY,{"disambiguationData":[OSD([sQuery(id+"F31.wireOp",EDGE,"E93.bottom"),sQuery(id+"F31.wireOp",EDGE,"E93.top"),sQuery(id+"F31.wireOp",EDGE,"E93.left"),sQuery(id+"F31.wireOp",EDGE,"E93.right")])]});
            hole(context, id + "F36", {"style" : HoleStyle.SIMPLE, "endStyle" : HoleEndStyle.BLIND, "holeDiameter" : 6.35 * mm, "majorDiameter" : 6.35 * mm, "holeDepth" : 19.05 * mm, "isTappedThrough" : true, "tappedDepth" : 12.7 * mm, "tapClearance" : 3, "locations" : qUnion([Q0, Q1]), "scope" : qUnion([Q2])});
        }
        {
            var Q0;
            Q0=sQuery(id+"F1.wireOp",VERTEX,"E26");
            var Q1;
            Q1=sQuery(id+"F1.wireOp",VERTEX,"E27");
            var Q2;
            Q2=makeQuery(id+"F3.opExtrude","SWEPT_BODY",BODY,{"disambiguationData":[OSD([sQuery(id+"F1.wireOp",EDGE,"E12.right"),sQuery(id+"F1.wireOp",EDGE,"E13.MirrorCS"),sQuery(id+"F1.wireOp",EDGE,"E14.MirrorCS"),sQuery(id+"F1.wireOp",EDGE,"E15.MirrorCS"),sQuery(id+"F1.wireOp",EDGE,"E16.MirrorCS"),sQuery(id+"F1.wireOp",EDGE,"E17.MirrorCS"),sQuery(id+"F1.wireOp",EDGE,"E18.MirrorCS"),sQuery(id+"F1.wireOp",EDGE,"E19.MirrorCS"),sQuery(id+"F1.wireOp",EDGE,"E20.MirrorCS"),sQuery(id+"F1.wireOp",EDGE,"E21.MirrorCS"),sQuery(id+"F1.wireOp",EDGE,"E22.MirrorCS"),sQuery(id+"F1.wireOp",EDGE,"E23")])]});
            hole(context, id + "F37", {"style" : HoleStyle.SIMPLE, "endStyle" : HoleEndStyle.THROUGH, "oppositeDirection" : true, "holeDiameter" : 6.35 * mm, "majorDiameter" : 6.35 * mm, "isTappedThrough" : true, "tappedDepth" : 12.7 * mm, "tapClearance" : 3, "locations" : qUnion([Q0, Q1]), "scope" : qUnion([Q2])});
        }
        {
            var Q0;
            Q0=qCreatedBy(makeId("Front.planeOp"),FACE);
            var sketch = newSketch(context, id + "F38", { "sketchPlane" : qUnion([Q0])});
            skLineSegment(sketch, "E105.bottom", {"start": v(-816.03, 183.72) * mm, "end": v(-209.6, 183.72) * mm});
            skLineSegment(sketch, "E105.top", {"start": v(-816.03, 94.82) * mm, "end": v(-209.6, 94.82) * mm});
            skLineSegment(sketch, "E105.left", {"start": v(-816.03, 183.72) * mm, "end": v(-816.03, 94.82) * mm});
            skLineSegment(sketch, "E105.right", {"start": v(-209.6, 183.72) * mm, "end": v(-209.6, 94.82) * mm});
            skSolve(sketch);
        }
        {
            var Q0;
            {var subQ0=sQuery(id+"F31.wireOp",EDGE,"E93.top");Q0=makeQuery(id+"F31.imprint","IMPRINT",FACE,{"disambiguationData":[TD([[makeQuery(id+"F31.imprint","IMPRINT",EDGE,{"derivedFrom":subQ0}),1.0]])]});}
            extrude(context, id + "F39", {"entities" : qUnion([Q0]), "operationType" : NewBodyOperationType.ADD, "depth" : 12.7 * mm, "offsetDistance" : 25.4 * mm});
        }
        {
            var Q0;
            Q0=sQuery(id+"F33.wireOp",VERTEX,"E100");
            var Q1;
            Q1=makeQuery(id+"F32.opExtrude","SWEPT_BODY",BODY,{"disambiguationData":[OSD([sQuery(id+"F31.wireOp",EDGE,"E93.bottom"),sQuery(id+"F31.wireOp",EDGE,"E93.left"),sQuery(id+"F31.wireOp",EDGE,"E93.right"),sQuery(id+"F31.wireOp",EDGE,"E95")])]});
            hole(context, id + "F40", {"style" : HoleStyle.SIMPLE, "endStyle" : HoleEndStyle.BLIND, "holeDiameter" : 6.35 * mm, "majorDiameter" : 6.35 * mm, "holeDepth" : 19.05 * mm, "isTappedThrough" : true, "tappedDepth" : 12.7 * mm, "tapClearance" : 3, "locations" : qUnion([Q0]), "scope" : qUnion([Q1])});
        }
        {
            var Q0;
            Q0=sQuery(id+"F35.wireOp",VERTEX,"E104");
            var Q1;
            Q1=makeQuery(id+"F32.opExtrude","SWEPT_BODY",BODY,{"disambiguationData":[OSD([sQuery(id+"F31.wireOp",EDGE,"E93.bottom"),sQuery(id+"F31.wireOp",EDGE,"E93.left"),sQuery(id+"F31.wireOp",EDGE,"E93.right"),sQuery(id+"F31.wireOp",EDGE,"E95")])]});
            hole(context, id + "F41", {"style" : HoleStyle.SIMPLE, "endStyle" : HoleEndStyle.BLIND, "holeDiameter" : 6.35 * mm, "majorDiameter" : 6.35 * mm, "holeDepth" : 19.05 * mm, "isTappedThrough" : true, "tappedDepth" : 12.7 * mm, "tapClearance" : 3, "locations" : qUnion([Q0]), "scope" : qUnion([Q1])});
        }
        {
            var Q0;
            Q0=makeQuery(id+"F38.imprint","IMPRINT",FACE,{"disambiguationData":[TD([[makeQuery(id+"F38.imprint","IMPRINT",EDGE,{"derivedFrom":sQuery(id+"F38.wireOp",EDGE,"E105.bottom")}),-1.0]])]});
            extrude(context, id + "F42", {"entities" : qUnion([Q0]), "depth" : 19.05 * mm, "offsetDistance" : 25.4 * mm});
        }
        {
            var Q0;
            Q0=makeQuery(id+"F42.opExtrude","SWEPT_FACE",FACE,{"disambiguationData":[OSD([sQuery(id+"F38.wireOp",EDGE,"E105.right")])]});
            var sketch = newSketch(context, id + "F43", { "sketchPlane" : qUnion([Q0])});
            skLineSegment(sketch, "E106.0.0", {"start": v(0, 94.82) * mm, "end": v(0, 183.72) * mm});
            skLineSegment(sketch, "E106.0.1", {"start": v(0, 183.72) * mm, "end": v(-19.05, 183.72) * mm});
            skLineSegment(sketch, "E106.0.2", {"start": v(-19.05, 183.72) * mm, "end": v(-19.05, 94.82) * mm});
            skLineSegment(sketch, "E106.0.3", {"start": v(-19.05, 94.82) * mm, "end": v(0, 94.82) * mm});
            skPoint(sketch, "E107", {"position": v(-9.53, 155.15) * mm});
            skPoint(sketch, "E107.positionSnap0", {"position": v(-9.53, 183.72) * mm});
            skPoint(sketch, "E108", {"position": v(-9.53, 123.4) * mm});
            skSolve(sketch);
        }
        {
            var Q0;
            Q0=sQuery(id+"F43.wireOp",VERTEX,"E107");
            var Q1;
            Q1=sQuery(id+"F43.wireOp",VERTEX,"E108");
            var Q2;
            Q2=makeQuery(id+"F42.opExtrude","SWEPT_BODY",BODY,{"disambiguationData":[OSD([sQuery(id+"F38.wireOp",EDGE,"E105.bottom"),sQuery(id+"F38.wireOp",EDGE,"E105.top"),sQuery(id+"F38.wireOp",EDGE,"E105.left"),sQuery(id+"F38.wireOp",EDGE,"E105.right")])]});
            hole(context, id + "F44", {"style" : HoleStyle.SIMPLE, "endStyle" : HoleEndStyle.BLIND, "holeDiameter" : 6.35 * mm, "majorDiameter" : 6.35 * mm, "holeDepth" : 19.05 * mm, "isTappedThrough" : true, "tappedDepth" : 12.7 * mm, "tapClearance" : 3, "locations" : qUnion([Q0, Q1]), "scope" : qUnion([Q2])});
        }
        {
            var Q0;
            Q0=makeQuery(id+"F42.opExtrude","SWEPT_FACE",FACE,{"disambiguationData":[OSD([sQuery(id+"F38.wireOp",EDGE,"E105.left")])]});
            var sketch = newSketch(context, id + "F45", { "sketchPlane" : qUnion([Q0])});
            skLineSegment(sketch, "E109.0.0", {"start": v(0, 183.72) * mm, "end": v(0, 94.82) * mm});
            skLineSegment(sketch, "E109.0.1", {"start": v(0, 94.82) * mm, "end": v(19.05, 94.82) * mm});
            skLineSegment(sketch, "E109.0.2", {"start": v(19.05, 94.82) * mm, "end": v(19.05, 183.72) * mm});
            skLineSegment(sketch, "E109.0.3", {"start": v(19.05, 183.72) * mm, "end": v(0, 183.72) * mm});
            skPoint(sketch, "E110", {"position": v(9.53, 155.15) * mm});
            skPoint(sketch, "E110.positionSnap0", {"position": v(9.53, 183.72) * mm});
            skPoint(sketch, "E111", {"position": v(9.52, 123.4) * mm});
            skPoint(sketch, "E111.positionSnap0", {"position": v(9.53, 94.82) * mm});
            skSolve(sketch);
        }
        {
            var Q0;
            Q0=sQuery(id+"F45.wireOp",VERTEX,"E110");
            var Q1;
            Q1=sQuery(id+"F45.wireOp",VERTEX,"E111");
            var Q2;
            Q2=makeQuery(id+"F42.opExtrude","SWEPT_BODY",BODY,{"disambiguationData":[OSD([sQuery(id+"F38.wireOp",EDGE,"E105.bottom"),sQuery(id+"F38.wireOp",EDGE,"E105.top"),sQuery(id+"F38.wireOp",EDGE,"E105.left"),sQuery(id+"F38.wireOp",EDGE,"E105.right")])]});
            hole(context, id + "F46", {"style" : HoleStyle.SIMPLE, "endStyle" : HoleEndStyle.BLIND, "holeDiameter" : 6.35 * mm, "majorDiameter" : 6.35 * mm, "holeDepth" : 19.05 * mm, "isTappedThrough" : true, "tappedDepth" : 12.7 * mm, "tapClearance" : 3, "locations" : qUnion([Q0, Q1]), "scope" : qUnion([Q2])});
        }
        {
            var Q0;
            Q0=qCreatedBy(makeId("Front.planeOp"),FACE);
            var sketch = newSketch(context, id + "F47", { "sketchPlane" : qUnion([Q0])});
            skLineSegment(sketch, "E112.bottom", {"start": v(-1005.43, 826.6) * mm, "end": v(950.37, 826.6) * mm});
            skLineSegment(sketch, "E112.top", {"start": v(-1005.43, 1125.05) * mm, "end": v(950.37, 1125.05) * mm});
            skLineSegment(sketch, "E112.left", {"start": v(-1005.43, 826.6) * mm, "end": v(-1005.43, 1125.05) * mm});
            skLineSegment(sketch, "E112.right", {"start": v(950.37, 826.6) * mm, "end": v(950.37, 1125.05) * mm});
            skPoint(sketch, "E113", {"position": v(-976.86, 874.22) * mm});
            skSolve(sketch);
        }
        {
            var Q0;
            Q0=makeQuery(id+"F47.imprint","IMPRINT",FACE,{"disambiguationData":[TD([[makeQuery(id+"F47.imprint","IMPRINT",EDGE,{"derivedFrom":sQuery(id+"F47.wireOp",EDGE,"E112.bottom")}),1.0]])]});
            extrude(context, id + "F48", {"entities" : qUnion([Q0]), "depth" : 19.05 * mm, "offsetDistance" : 25.4 * mm});
        }
        {
            var Q0;
            Q0=sQuery(id+"F47.wireOp",VERTEX,"E113");
            var Q1;
            Q1=makeQuery(id+"F48.opExtrude","SWEPT_BODY",BODY,{"disambiguationData":[OSD([sQuery(id+"F47.wireOp",EDGE,"E112.bottom"),sQuery(id+"F47.wireOp",EDGE,"E112.top"),sQuery(id+"F47.wireOp",EDGE,"E112.left"),sQuery(id+"F47.wireOp",EDGE,"E112.right")])]});
            hole(context, id + "F49", {"style" : HoleStyle.SIMPLE, "endStyle" : HoleEndStyle.BLIND, "oppositeDirection" : true, "holeDiameter" : 6.35 * mm, "majorDiameter" : 6.35 * mm, "holeDepth" : 12.7 * mm, "isTappedThrough" : true, "tappedDepth" : 12.7 * mm, "tapClearance" : 3, "locations" : qUnion([Q0]), "scope" : qUnion([Q1])});
        }
        {
            var Q0;
            Q0=qCreatedBy(makeId("Front.planeOp"),FACE);
            var sketch = newSketch(context, id + "F50", { "sketchPlane" : qUnion([Q0])});
            skLineSegment(sketch, "E114.bottom", {"start": v(-626.9, 492.4) * mm, "end": v(-1255.55, 492.4) * mm});
            skLineSegment(sketch, "E114.top", {"start": v(-626.9, 352.7) * mm, "end": v(-1255.55, 352.7) * mm});
            skLineSegment(sketch, "E114.left", {"start": v(-626.9, 492.4) * mm, "end": v(-626.9, 352.7) * mm});
            skLineSegment(sketch, "E114.right", {"start": v(-1255.55, 492.4) * mm, "end": v(-1255.55, 352.7) * mm});
            skSolve(sketch);
        }
        {
            var Q0;
            Q0 = qSketchRegion(id + "F50", true);
            var Q1;
            Q1=makeQuery(id+"F50.imprint","IMPRINT",FACE,{"disambiguationData":[TD([[makeQuery(id+"F50.imprint","IMPRINT",EDGE,{"derivedFrom":sQuery(id+"F50.wireOp",EDGE,"E114.bottom")}),1.0]])]});
            extrude(context, id + "F51", {"entities" : qUnion([Q0, Q1]), "depth" : 19.05 * mm, "offsetDistance" : 25.4 * mm});
        }
        {
            var Q0;
            Q0=qCreatedBy(makeId("Front.planeOp"),FACE);
            var sketch = newSketch(context, id + "F52", { "sketchPlane" : qUnion([Q0])});
            skLineSegment(sketch, "E115.bottom", {"start": v(687.6, 338.95) * mm, "end": v(1316.25, 338.95) * mm});
            skLineSegment(sketch, "E115.top", {"start": v(687.6, -175.4) * mm, "end": v(1316.25, -175.4) * mm});
            skLineSegment(sketch, "E115.left", {"start": v(687.6, 338.95) * mm, "end": v(687.6, -175.4) * mm});
            skLineSegment(sketch, "E115.right", {"start": v(1316.25, 338.95) * mm, "end": v(1316.25, -175.4) * mm});
            skSolve(sketch);
        }
        {
            var Q0;
            Q0=makeQuery(id+"F52.imprint","IMPRINT",FACE,{"disambiguationData":[TD([[makeQuery(id+"F52.imprint","IMPRINT",EDGE,{"derivedFrom":sQuery(id+"F52.wireOp",EDGE,"E115.bottom")}),-1.0]])]});
            extrude(context, id + "F53", {"entities" : qUnion([Q0]), "depth" : 6.35 * mm, "offsetDistance" : 25.4 * mm});
        }
        {
            var Q0;
            Q0=qCreatedBy(makeId("Front.planeOp"),FACE);
            var sketch = newSketch(context, id + "F54", { "sketchPlane" : qUnion([Q0])});
            skLineSegment(sketch, "E116.bottom", {"start": v(694.68, -279) * mm, "end": v(1301.1, -279) * mm});
            skLineSegment(sketch, "E116.top", {"start": v(694.68, -793.35) * mm, "end": v(1301.1, -793.35) * mm});
            skLineSegment(sketch, "E116.left", {"start": v(694.68, -279) * mm, "end": v(694.68, -793.35) * mm});
            skLineSegment(sketch, "E116.right", {"start": v(1301.1, -279) * mm, "end": v(1301.1, -793.35) * mm});
            skSolve(sketch);
        }
        {
            var Q0;
            Q0=makeQuery(id+"F54.imprint","IMPRINT",FACE,{"disambiguationData":[TD([[makeQuery(id+"F54.imprint","IMPRINT",EDGE,{"derivedFrom":sQuery(id+"F54.wireOp",EDGE,"E116.bottom")}),-1.0]])]});
            extrude(context, id + "F55", {"entities" : qUnion([Q0]), "depth" : 6.35 * mm, "offsetDistance" : 25.4 * mm});
        }
        {
            var Q0;
            Q0=qCreatedBy(makeId("Front.planeOp"),FACE);
            var sketch = newSketch(context, id + "F56", { "sketchPlane" : qUnion([Q0])});
            skLineSegment(sketch, "E117.bottom", {"start": v(-1234.48, 33.42) * mm, "end": v(-589.95, 33.42) * mm});
            skLineSegment(sketch, "E117.top", {"start": v(-1234.48, -106.28) * mm, "end": v(-589.95, -106.28) * mm});
            skLineSegment(sketch, "E117.left", {"start": v(-1234.48, 33.42) * mm, "end": v(-1234.48, -106.28) * mm});
            skLineSegment(sketch, "E117.right", {"start": v(-589.95, 33.42) * mm, "end": v(-589.95, -106.28) * mm});
            skSolve(sketch);
        }
        {
            var Q0;
            Q0 = qSketchRegion(id + "F56", true);
            extrude(context, id + "F57", {"entities" : qUnion([Q0]), "depth" : 19.05 * mm, "offsetDistance" : 25.4 * mm});
        }
    });
